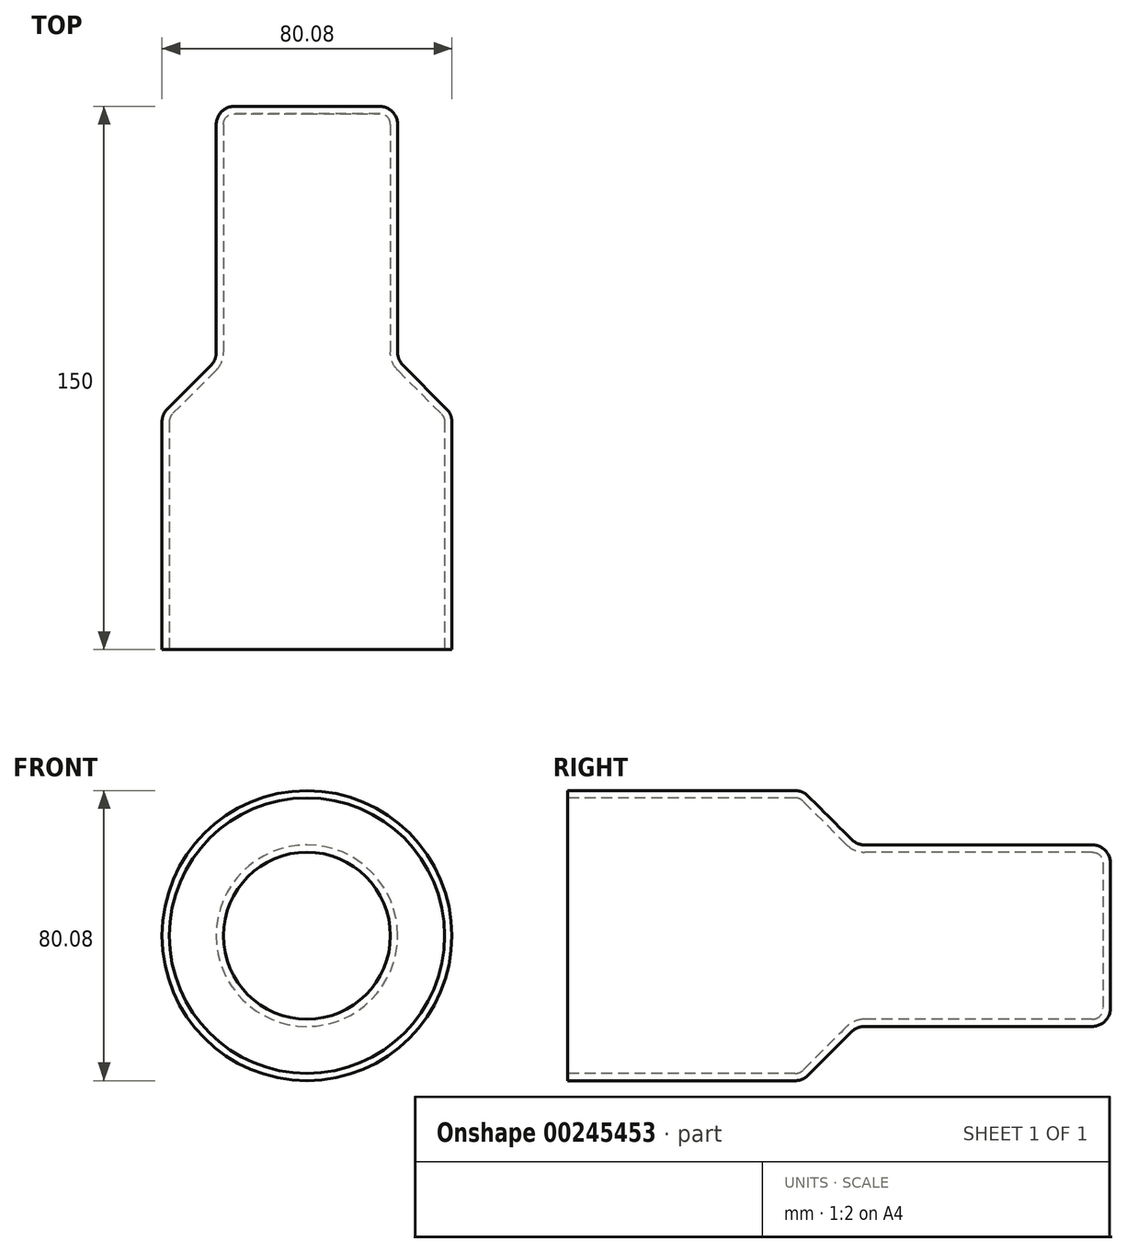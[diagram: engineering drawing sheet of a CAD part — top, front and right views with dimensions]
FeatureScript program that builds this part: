
annotation { "Feature Type Name" : "Feature", "Feature Type Description" : "" }
export const myFeature = defineFeature(function(context is Context, id is Id, definition is map)
    precondition{}
    {
        {
            var Q0;
            Q0=qCreatedBy(makeId("Front.planeOp"),FACE);
            var sketch = newSketch(context, id + "F0", { "sketchPlane" : qUnion([Q0])});
            skCircle(sketch, "E0", {"center": v(0, 0) * mm, "radius": 40.04 * mm});
            skSolve(sketch);
        }
        {
            var Q0;
            Q0=makeQuery(id+"F0.imprint","IMPRINT",FACE,{"disambiguationData":[TD([[makeQuery(id+"F0.imprint","IMPRINT",EDGE,{"derivedFrom":sQuery(id+"F0.wireOp",EDGE,"E0")}),1.0]])]});
            var Q1;
            Q1=sQuery(id+"F0.wireOp",EDGE,"E0");
            extrude(context, id + "F1", {"entities" : qUnion([Q0]), "surfaceEntities" : qUnion([Q1]), "oppositeDirection" : true, "depth" : 80 * mm});
        }
        {
            var Q0;
            Q0=makeQuery(id+"F1.opExtrude","CAP_FACE",FACE,{"disambiguationData":[OSD([sQuery(id+"F0.wireOp",EDGE,"E0")])],"isStart":false});
            var sketch = newSketch(context, id + "F2", { "sketchPlane" : qUnion([Q0])});
            skCircle(sketch, "E1", {"center": v(0, 0) * mm, "radius": 25.07 * mm});
            skSolve(sketch);
        }
        {
            var Q0;
            Q0=makeQuery(id+"F2.imprint","IMPRINT",FACE,{"disambiguationData":[TD([[makeQuery(id+"F2.imprint","IMPRINT",EDGE,{"derivedFrom":sQuery(id+"F2.wireOp",EDGE,"E1")}),1.0]])]});
            extrude(context, id + "F3", {"entities" : qUnion([Q0]), "operationType" : NewBodyOperationType.ADD, "depth" : 70 * mm});
        }
        {
            var Q0;
            Q0=makeQuery(id+"F1.opExtrude","CAP_EDGE",EDGE,{"disambiguationData":[OSD([sQuery(id+"F0.wireOp",EDGE,"E0")])],"isStart":false});
            chamfer(context, id + "F4", {"entities" : qUnion([Q0]), "width" : 15 * mm, "tangentPropagation" : true});
        }
        {
            var Q0;
            Q0=makeQuery(id+"F3.opExtrude","CAP_FACE",FACE,{"disambiguationData":[OSD([sQuery(id+"F2.wireOp",EDGE,"E1")])],"isStart":false});
            fillet(context, id + "F5", {"entities" : qUnion([Q0]), "radius" : 5 * mm, "tangentPropagation" : true, "allowEdgeOverflow" : false});
        }
        {
            var Q0;
            Q0=makeQuery(id+"F4.opChamfer","BLEND_FACE",FACE,{"disambiguationData":[OSD([sQuery(id+"F0.wireOp",EDGE,"E0")])]});
            fillet(context, id + "F6", {"entities" : qUnion([Q0]), "radius" : 5 * mm, "tangentPropagation" : true, "allowEdgeOverflow" : false});
        }
        {
            var Q0;
            Q0=makeQuery(id+"F1.opExtrude","CAP_FACE",FACE,{"disambiguationData":[OSD([sQuery(id+"F0.wireOp",EDGE,"E0")])],"isStart":true});
            shell(context, id + "F7", {"entities" : qUnion([Q0]), "thickness" : 2 * mm});
        }
    });
